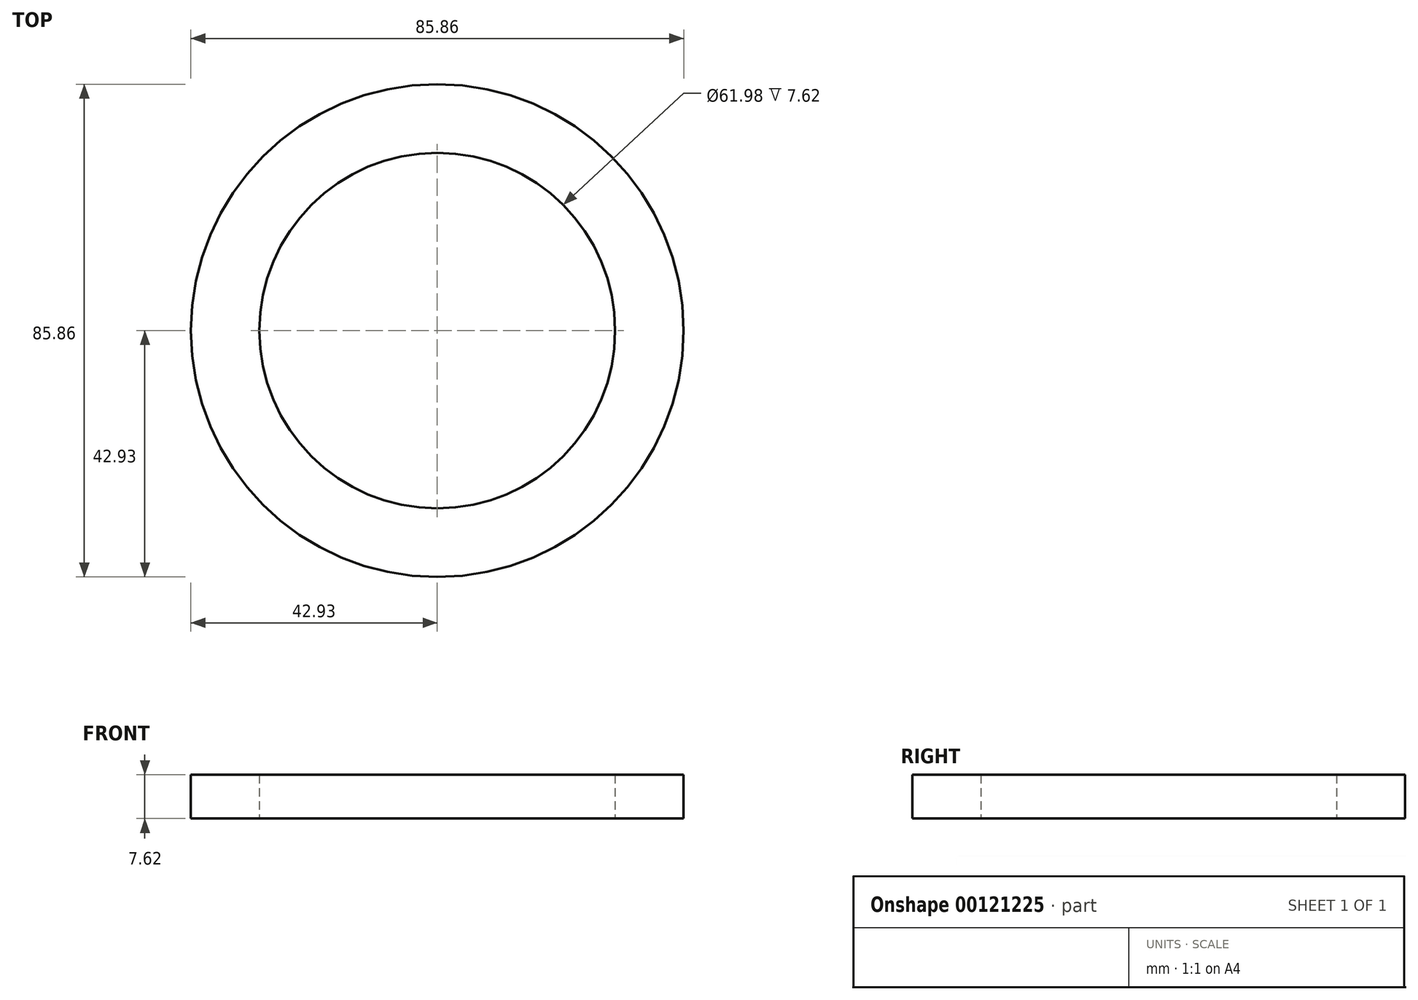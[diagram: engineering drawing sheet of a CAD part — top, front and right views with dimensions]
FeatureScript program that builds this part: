
annotation { "Feature Type Name" : "Feature", "Feature Type Description" : "" }
export const myFeature = defineFeature(function(context is Context, id is Id, definition is map)
    precondition{}
    {
        {
            var Q0;
            Q0=qCreatedBy(makeId("Top.planeOp"),FACE);
            var sketch = newSketch(context, id + "F0", { "sketchPlane" : qUnion([Q0])});
            skCircle(sketch, "E0", {"center": v(0, 0) * mm, "radius": 42.93 * mm});
            skCircle(sketch, "E1", {"center": v(0, 0) * mm, "radius": 30.99 * mm});
            skSolve(sketch);
        }
        {
            var Q0;
            Q0=makeQuery(id+"F0.imprint","IMPRINT",FACE,{"disambiguationData":[TD([[makeQuery(id+"F0.imprint","IMPRINT",EDGE,{"derivedFrom":sQuery(id+"F0.wireOp",EDGE,"E0")}),1.0]])]});
            extrude(context, id + "F1", {"entities" : qUnion([Q0]), "depth" : 7.62 * mm});
        }
    });
